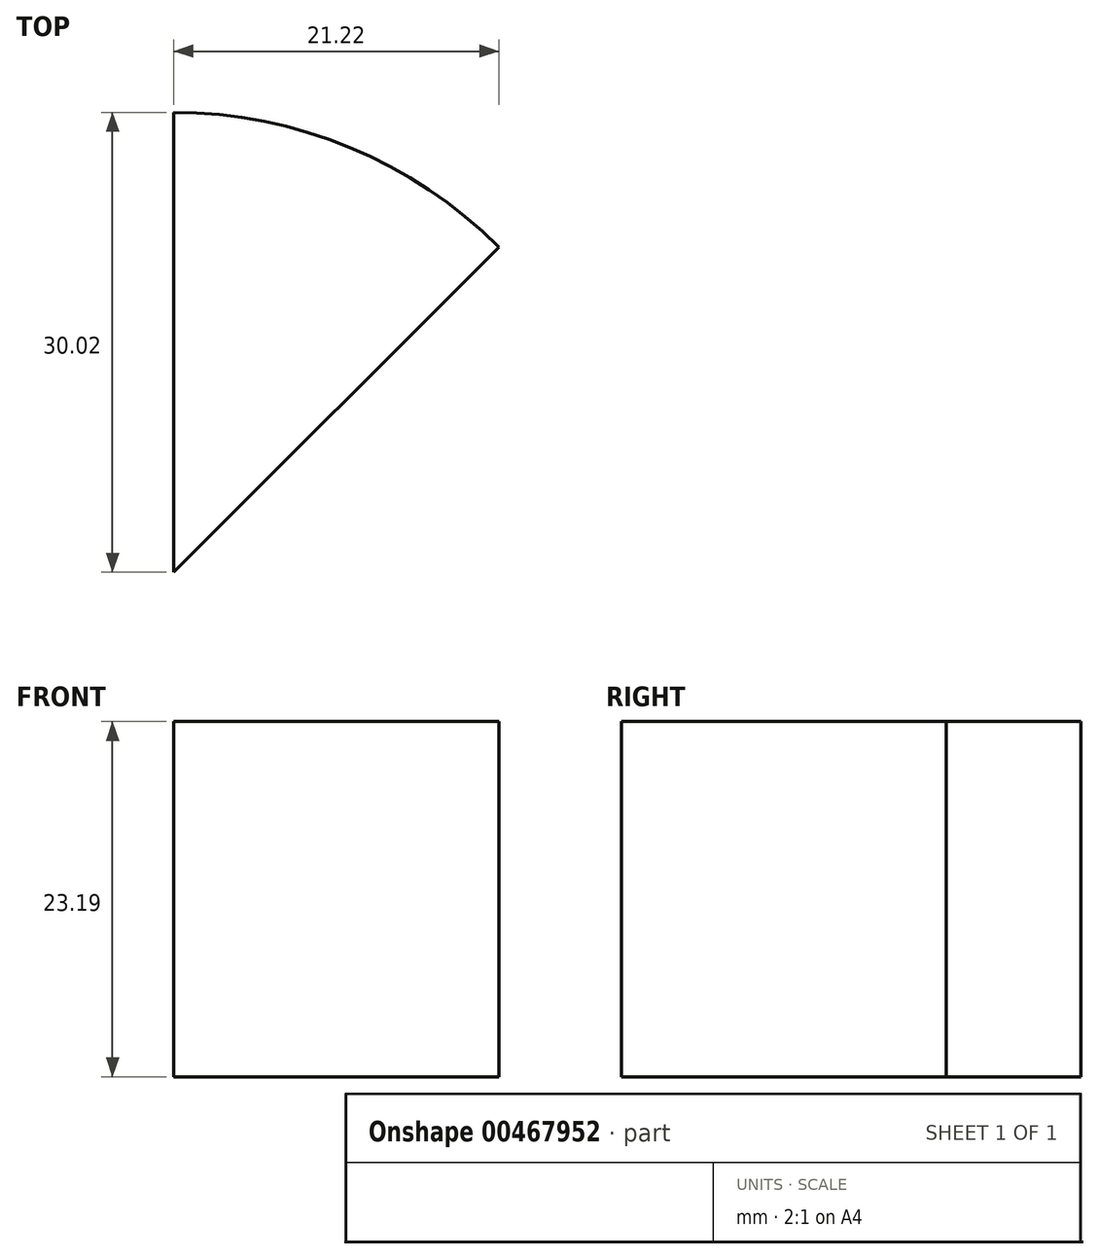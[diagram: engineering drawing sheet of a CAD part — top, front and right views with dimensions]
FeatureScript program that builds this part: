
annotation { "Feature Type Name" : "Feature", "Feature Type Description" : "" }
export const myFeature = defineFeature(function(context is Context, id is Id, definition is map)
    precondition{}
    {
        {
            var Q0;
            Q0=qCreatedBy(makeId("Right.planeOp"),FACE);
            var sketch = newSketch(context, id + "F0", { "sketchPlane" : qUnion([Q0])});
            skLineSegment(sketch, "E0.bottom", {"start": v(17.67, 44.14) * mm, "end": v(47.69, 44.14) * mm});
            skLineSegment(sketch, "E0.top", {"start": v(17.67, 20.95) * mm, "end": v(47.69, 20.95) * mm});
            skLineSegment(sketch, "E0.left", {"start": v(17.67, 44.14) * mm, "end": v(17.67, 20.95) * mm});
            skLineSegment(sketch, "E0.right", {"start": v(47.69, 44.14) * mm, "end": v(47.69, 20.95) * mm});
            skSolve(sketch);
        }
        {
            var Q0;
            Q0=makeQuery(id+"F0.imprint","IMPRINT",FACE,{"disambiguationData":[TD([[makeQuery(id+"F0.imprint","IMPRINT",EDGE,{"derivedFrom":sQuery(id+"F0.wireOp",EDGE,"E0.bottom")}),-1.0]])]});
            var Q1;
            Q1=sQuery(id+"F0.wireOp",EDGE,"E0.left");
            revolve(context, id + "F1", {"entities" : qUnion([Q0]), "axis" : qUnion([Q1]), "revolveType" : RevolveType.ONE_DIRECTION, "angle" : 45 * degree});
        }
    });
